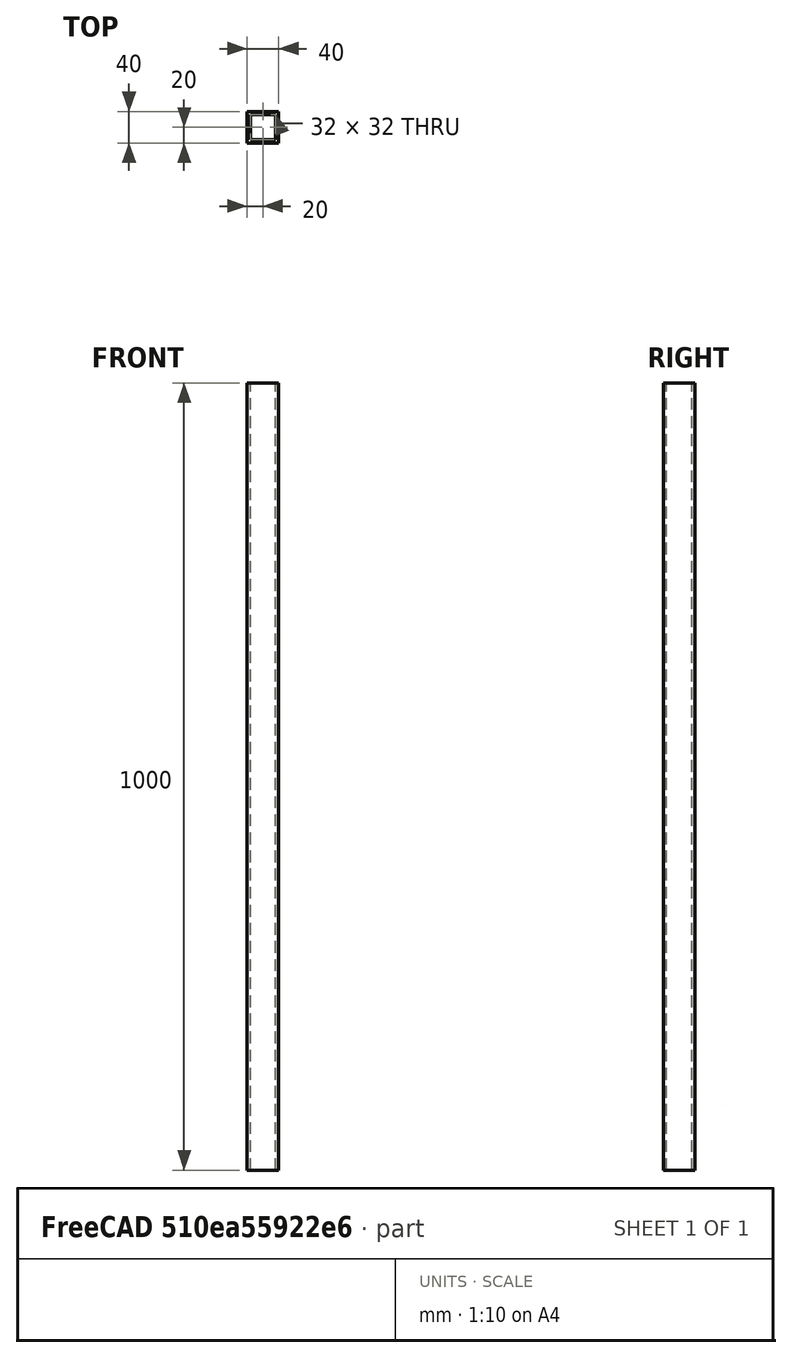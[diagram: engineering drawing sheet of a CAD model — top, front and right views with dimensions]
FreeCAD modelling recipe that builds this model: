
FCSTD DOCUMENT  (FreeCAD 0.15R4671 (Git))
Label: support profilé cadre
License: All rights reserved
LicenseURL: http://fr.wikipedia.org/wiki/<copyright redacted>
objects: Sketcher::SketchObject×1, PartDesign::Pad×1
note: 3 computed .brp shape members not serialized (recipe doc carries the construction recipe); baked Part::Feature solids carry a one-line shape summary decoded from their .brp

FEATURE [Sketcher::SketchObject] Sketch
  sketch-geometry (15):
    g0: LineSegment StartX=-16 StartY=16 StartZ=0 EndX=16 EndY=16 EndZ=0
    g1: LineSegment StartX=16 StartY=16 StartZ=0 EndX=16 EndY=-16 EndZ=0
    g2: LineSegment StartX=16 StartY=-16 StartZ=0 EndX=-16 EndY=-16 EndZ=0
    g3: LineSegment StartX=-16 StartY=-16 StartZ=0 EndX=-16 EndY=16 EndZ=0
    g4: LineSegment StartX=-20 StartY=20 StartZ=0 EndX=20 EndY=20 EndZ=0
    g5: LineSegment StartX=20 StartY=20 StartZ=0 EndX=20 EndY=-20 EndZ=0
    g6: LineSegment StartX=20 StartY=-20 StartZ=0 EndX=-20 EndY=-20 EndZ=0
    g7: LineSegment StartX=-20 StartY=-20 StartZ=0 EndX=-20 EndY=20 EndZ=0
    g8: LineSegment [constr] StartX=-16 StartY=16 StartZ=0 EndX=0 EndY=0 EndZ=0
    g9: LineSegment [constr] StartX=0 StartY=0 StartZ=0 EndX=16 EndY=16 EndZ=0
    g10: LineSegment [constr] StartX=-20 StartY=20 StartZ=0 EndX=-16 EndY=16 EndZ=0
    g11: LineSegment [constr] StartX=20 StartY=20 StartZ=0 EndX=16 EndY=16 EndZ=0
    g12: LineSegment [constr] StartX=-20 StartY=-20 StartZ=0 EndX=-16 EndY=-16 EndZ=0
    g13: LineSegment [constr] StartX=16 StartY=-16 StartZ=0 EndX=20 EndY=-20 EndZ=0
    g14: LineSegment [constr] StartX=0 StartY=0 StartZ=0 EndX=-16 EndY=-16 EndZ=0
  constraints (38):
    c: Coincident(g0,g1)
    c: Coincident(g1,g2)
    c: Coincident(g2,g3)
    c: Coincident(g3,g0)
    c: Horizontal(g0)
    c: Horizontal(g2)
    c: Vertical(g1)
    c: Vertical(g3)
    c: Coincident(g4,g5)
    c: Coincident(g5,g6)
    c: Coincident(g6,g7)
    c: Coincident(g7,g4)
    c: Horizontal(g4)
    c: Horizontal(g6)
    c: Vertical(g5)
    c: Vertical(g7)
    c: Coincident(g8,g0)
    c: Coincident(g8,g-1)
    c: Coincident(g9,g-1)
    c: Coincident(g9,g0)
    c: Coincident(g10,g4)
    c: Coincident(g10,g0)
    c: Coincident(g11,g4)
    c: Coincident(g11,g0)
    c: Equal(g8,g9)
    c: Coincident(g12,g6)
    c: Coincident(g12,g2)
    c: Coincident(g13,g1)
    c: Coincident(g13,g5)
    c: Equal(g12,g10)
    c: Equal(g10,g11)
    c: Equal(g4,g7)
    c: Equal(g0,g3)
    c: Distance(g4) = 40
    c: Distance(g0) = 32
    c: Coincident(g14,g-1)
    c: Coincident(g14,g2)
    c: Equal(g14,g8)
FEATURE [PartDesign::Pad] Pad
  Length = 1000
  Length2 = 100
  Sketch = -> Sketch
  Type = 0
